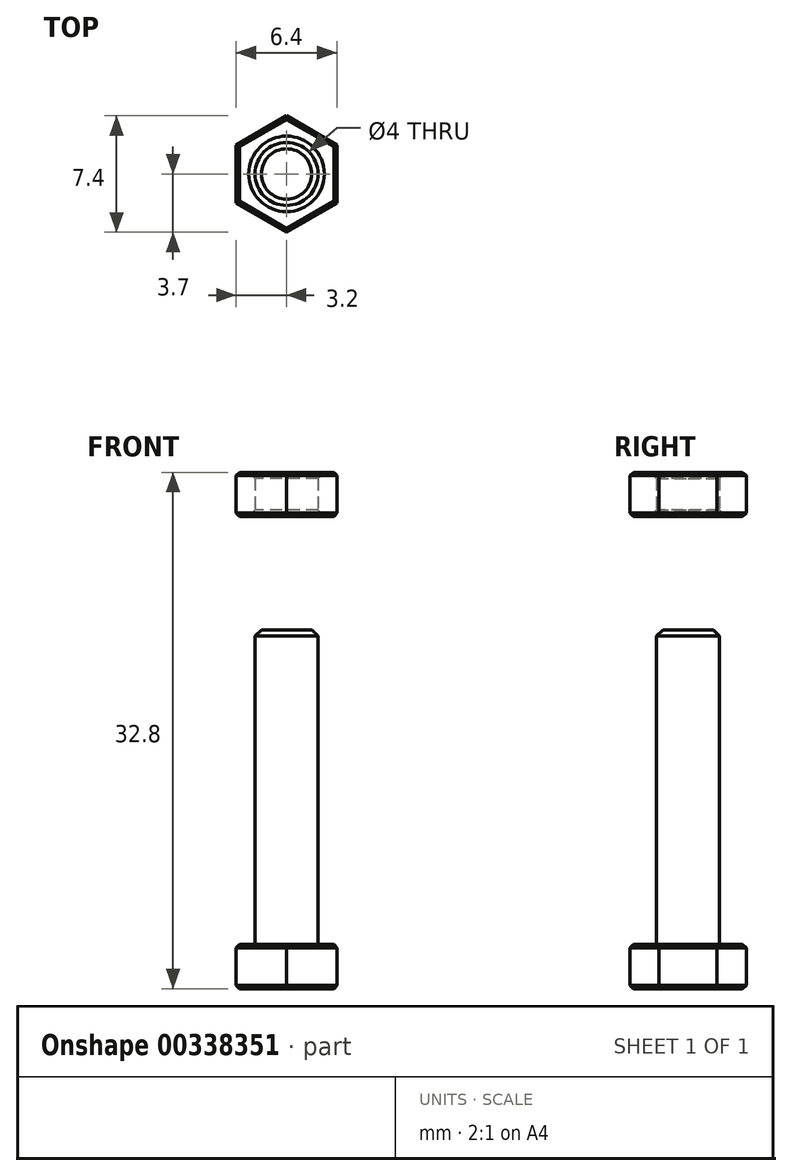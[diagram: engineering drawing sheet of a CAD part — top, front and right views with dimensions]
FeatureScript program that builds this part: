
annotation { "Feature Type Name" : "Feature", "Feature Type Description" : "" }
export const myFeature = defineFeature(function(context is Context, id is Id, definition is map)
    precondition{}
    {
        {
            assignVariable(context, id + "F0", {"name" : "ScrewSize", "anyValue" : 4});
        }
        {
            assignVariable(context, id + "F1", {"name" : "ScrewLength", "anyValue" : 20});
        }
        {
            var Q0;
            Q0=qCreatedBy(makeId("Top.planeOp"),FACE);
            var sketch = newSketch(context, id + "F2", { "sketchPlane" : qUnion([Q0])});
            skCircle(sketch, "E0.cCircle", {"center": v(0, 0) * mm, "radius": 3.2 * mm, "construction": true});
            skLineSegment(sketch, "E0.0", {"start": v(3.2, -1.85) * mm, "end": v(0, -3.7) * mm});
            skLineSegment(sketch, "E0.1", {"start": v(0, -3.7) * mm, "end": v(-3.2, -1.85) * mm});
            skLineSegment(sketch, "E0.2", {"start": v(-3.2, -1.85) * mm, "end": v(-3.2, 1.85) * mm});
            skLineSegment(sketch, "E0.3", {"start": v(-3.2, 1.85) * mm, "end": v(0, 3.7) * mm});
            skLineSegment(sketch, "E0.4", {"start": v(0, 3.7) * mm, "end": v(3.2, 1.85) * mm});
            skLineSegment(sketch, "E0.5", {"start": v(3.2, 1.85) * mm, "end": v(3.2, -1.85) * mm});
            skPoint(sketch, "E0.0.midPoint", {"position": v(1.6, -2.77) * mm});
            skSolve(sketch);
        }
        {
            var Q0;
            Q0 = qSketchRegion(id + "F2", true);
            extrude(context, id + "F3", {"entities" : qUnion([Q0]), "depth" : (0.7 * getVariable(context, 'ScrewSize')) * mm});
        }
        {
            var Q0;
            Q0=makeQuery(id+"F3.opExtrude","CAP_FACE",FACE,{"disambiguationData":[OSD([sQuery(id+"F2.wireOp",EDGE,"E0.0"),sQuery(id+"F2.wireOp",EDGE,"E0.1"),sQuery(id+"F2.wireOp",EDGE,"E0.2"),sQuery(id+"F2.wireOp",EDGE,"E0.3"),sQuery(id+"F2.wireOp",EDGE,"E0.4"),sQuery(id+"F2.wireOp",EDGE,"E0.5")])],"isStart":false});
            var sketch = newSketch(context, id + "F4", { "sketchPlane" : qUnion([Q0])});
            skCircle(sketch, "E1", {"center": v(0, 0) * mm, "radius": 2 * mm});
            skSolve(sketch);
        }
        {
            var Q0;
            Q0 = qSketchRegion(id + "F4", true);
            extrude(context, id + "F5", {"entities" : qUnion([Q0]), "operationType" : NewBodyOperationType.ADD, "depth" : (getVariable(context, 'ScrewLength')) * mm});
        }
        {
            var Q0;
            Q0=qCreatedBy(makeId("Top.planeOp"),FACE);
            cPlane(context, id + "F6", {"entities" : qUnion([Q0]), "cplaneType" : CPlaneType.OFFSET, "offset" : (getVariable(context, 'ScrewLength') + 10) * mm, "width" : 150 * mm, "height" : 150 * mm});
        }
        {
            var Q0;
            Q0=qCreatedBy(id+"F6.planeOp",FACE);
            var sketch = newSketch(context, id + "F7", { "sketchPlane" : qUnion([Q0])});
            skLineSegment(sketch, "E2.0.0", {"start": v(3.2, -1.85) * mm, "end": v(3.2, 1.85) * mm});
            skLineSegment(sketch, "E2.0.1", {"start": v(3.2, 1.85) * mm, "end": v(0, 3.7) * mm});
            skLineSegment(sketch, "E2.0.2", {"start": v(0, 3.7) * mm, "end": v(-3.2, 1.85) * mm});
            skLineSegment(sketch, "E2.0.3", {"start": v(-3.2, 1.85) * mm, "end": v(-3.2, -1.85) * mm});
            skLineSegment(sketch, "E2.0.4", {"start": v(-3.2, -1.85) * mm, "end": v(0, -3.7) * mm});
            skLineSegment(sketch, "E2.0.5", {"start": v(0, -3.7) * mm, "end": v(3.2, -1.85) * mm});
            skCircle(sketch, "E3.0.0", {"center": v(0, 0) * mm, "radius": 2 * mm});
            skSolve(sketch);
        }
        {
            var Q0;
            Q0 = qSketchRegion(id + "F7", true);
            extrude(context, id + "F8", {"entities" : qUnion([Q0]), "depth" : (0.7 * getVariable(context, 'ScrewSize')) * mm});
        }
        {
            var Q0;
            Q0=makeQuery(id+"F3.opExtrude","CAP_FACE",FACE,{"disambiguationData":[OSD([sQuery(id+"F2.wireOp",EDGE,"E0.0"),sQuery(id+"F2.wireOp",EDGE,"E0.1"),sQuery(id+"F2.wireOp",EDGE,"E0.2"),sQuery(id+"F2.wireOp",EDGE,"E0.3"),sQuery(id+"F2.wireOp",EDGE,"E0.4"),sQuery(id+"F2.wireOp",EDGE,"E0.5")])],"isStart":true});
            var Q1;
            Q1=makeQuery(id+"F3.opExtrude","CAP_EDGE",EDGE,{"disambiguationData":[OSD([sQuery(id+"F2.wireOp",EDGE,"E0.2")])],"isStart":false});
            var Q2;
            Q2=makeQuery(id+"F3.opExtrude","CAP_EDGE",EDGE,{"disambiguationData":[OSD([sQuery(id+"F2.wireOp",EDGE,"E0.1")])],"isStart":false});
            var Q3;
            Q3=makeQuery(id+"F3.opExtrude","CAP_EDGE",EDGE,{"disambiguationData":[OSD([sQuery(id+"F2.wireOp",EDGE,"E0.0")])],"isStart":false});
            var Q4;
            Q4=makeQuery(id+"F3.opExtrude","CAP_EDGE",EDGE,{"disambiguationData":[OSD([sQuery(id+"F2.wireOp",EDGE,"E0.3")])],"isStart":false});
            var Q5;
            Q5=makeQuery(id+"F3.opExtrude","CAP_EDGE",EDGE,{"disambiguationData":[OSD([sQuery(id+"F2.wireOp",EDGE,"E0.4")])],"isStart":false});
            var Q6;
            Q6=makeQuery(id+"F3.opExtrude","CAP_EDGE",EDGE,{"disambiguationData":[OSD([sQuery(id+"F2.wireOp",EDGE,"E0.5")])],"isStart":false});
            var Q7;
            Q7=makeQuery(id+"F8.opExtrude","CAP_EDGE",EDGE,{"disambiguationData":[OSD([sQuery(id+"F7.wireOp",EDGE,"E2.0.1")])],"isStart":false});
            var Q8;
            Q8=makeQuery(id+"F8.opExtrude","CAP_EDGE",EDGE,{"disambiguationData":[OSD([sQuery(id+"F7.wireOp",EDGE,"E2.0.2")])],"isStart":false});
            var Q9;
            Q9=makeQuery(id+"F8.opExtrude","CAP_EDGE",EDGE,{"disambiguationData":[OSD([sQuery(id+"F7.wireOp",EDGE,"E2.0.3")])],"isStart":false});
            var Q10;
            Q10=makeQuery(id+"F8.opExtrude","CAP_EDGE",EDGE,{"disambiguationData":[OSD([sQuery(id+"F7.wireOp",EDGE,"E2.0.4")])],"isStart":false});
            var Q11;
            Q11=makeQuery(id+"F8.opExtrude","CAP_EDGE",EDGE,{"disambiguationData":[OSD([sQuery(id+"F7.wireOp",EDGE,"E2.0.5")])],"isStart":false});
            var Q12;
            Q12=makeQuery(id+"F8.opExtrude","CAP_EDGE",EDGE,{"disambiguationData":[OSD([sQuery(id+"F7.wireOp",EDGE,"E2.0.0")])],"isStart":false});
            var Q13;
            Q13=makeQuery(id+"F8.opExtrude","CAP_EDGE",EDGE,{"disambiguationData":[OSD([sQuery(id+"F7.wireOp",EDGE,"E2.0.5")])],"isStart":true});
            var Q14;
            Q14=makeQuery(id+"F8.opExtrude","CAP_EDGE",EDGE,{"disambiguationData":[OSD([sQuery(id+"F7.wireOp",EDGE,"E2.0.4")])],"isStart":true});
            var Q15;
            Q15=makeQuery(id+"F8.opExtrude","CAP_EDGE",EDGE,{"disambiguationData":[OSD([sQuery(id+"F7.wireOp",EDGE,"E2.0.3")])],"isStart":true});
            var Q16;
            Q16=makeQuery(id+"F8.opExtrude","CAP_EDGE",EDGE,{"disambiguationData":[OSD([sQuery(id+"F7.wireOp",EDGE,"E2.0.2")])],"isStart":true});
            var Q17;
            Q17=makeQuery(id+"F8.opExtrude","CAP_EDGE",EDGE,{"disambiguationData":[OSD([sQuery(id+"F7.wireOp",EDGE,"E2.0.1")])],"isStart":true});
            var Q18;
            Q18=makeQuery(id+"F8.opExtrude","CAP_EDGE",EDGE,{"disambiguationData":[OSD([sQuery(id+"F7.wireOp",EDGE,"E2.0.0")])],"isStart":true});
            chamfer(context, id + "F9", {"entities" : qUnion([Q0, Q1, Q2, Q3, Q4, Q5, Q6, Q7, Q8, Q9, Q10, Q11, Q12, Q13, Q14, Q15, Q16, Q17, Q18]), "chamferType" : ChamferType.OFFSET_ANGLE, "width" : 0.2 * mm, "oppositeDirection" : false, "angle" : 45 * degree, "tangentPropagation" : true});
        }
        {
            var Q0;
            Q0=makeQuery(id+"F5.opExtrude","CAP_FACE",FACE,{"disambiguationData":[OSD([sQuery(id+"F4.wireOp",EDGE,"E1")])],"isStart":false});
            var Q1;
            Q1=makeQuery(id+"F8.opExtrude","SWEPT_FACE",FACE,{"disambiguationData":[OSD([sQuery(id+"F7.wireOp",EDGE,"E3.0.0")])]});
            chamfer(context, id + "F10", {"entities" : qUnion([Q0, Q1]), "width" : 0.4 * mm, "tangentPropagation" : true});
        }
    });
